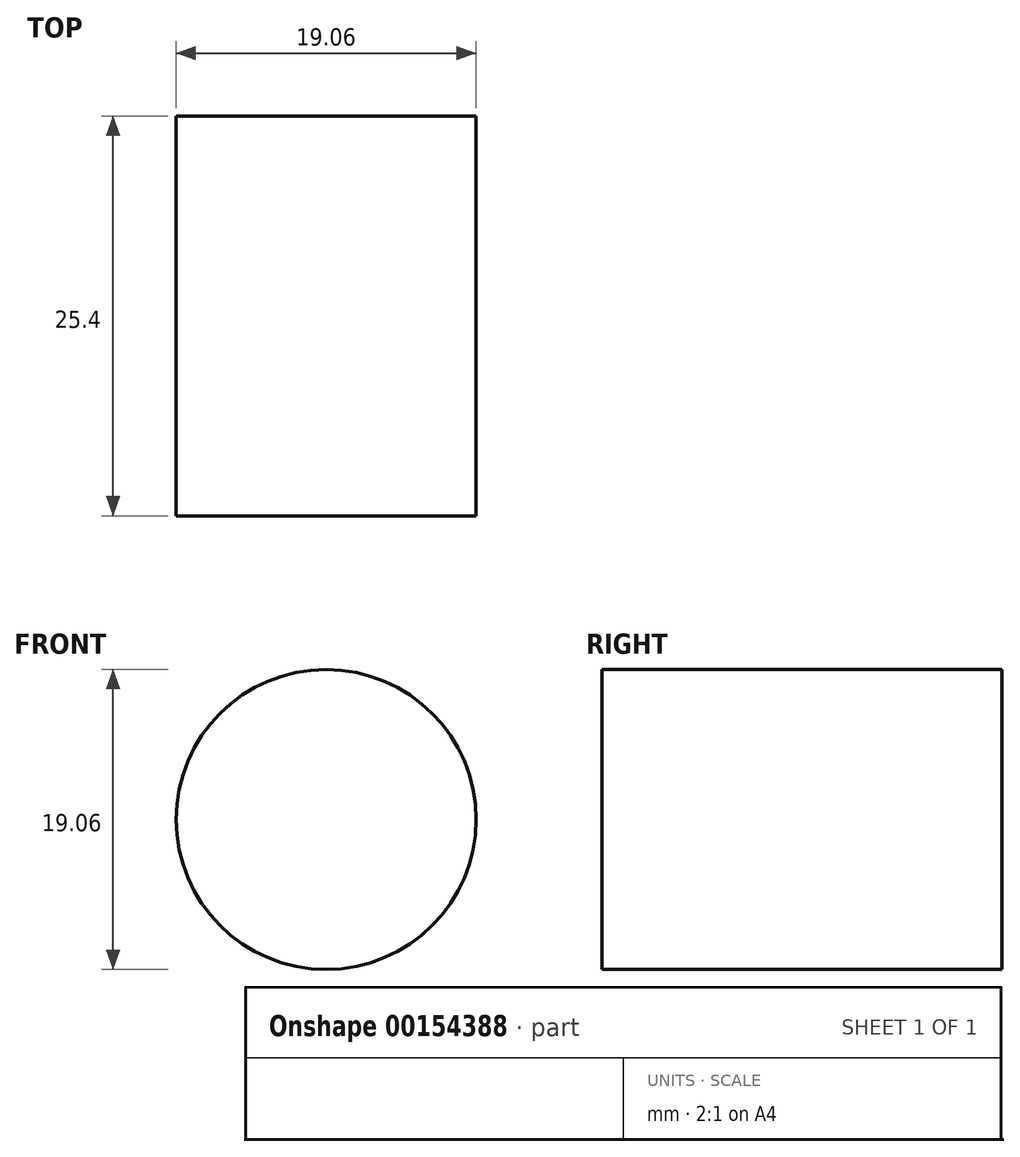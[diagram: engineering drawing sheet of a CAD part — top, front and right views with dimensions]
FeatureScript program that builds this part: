
annotation { "Feature Type Name" : "Feature", "Feature Type Description" : "" }
export const myFeature = defineFeature(function(context is Context, id is Id, definition is map)
    precondition{}
    {
        {
            var Q0;
            Q0=qCreatedBy(makeId("Front.planeOp"),FACE);
            var sketch = newSketch(context, id + "F0", { "sketchPlane" : qUnion([Q0])});
            skCircle(sketch, "E0", {"center": v(0, 0) * mm, "radius": 9.53 * mm});
            skSolve(sketch);
        }
        {
            var Q0;
            Q0=makeQuery(id+"F0.imprint","IMPRINT",FACE,{"disambiguationData":[TD([[makeQuery(id+"F0.imprint","IMPRINT",EDGE,{"derivedFrom":sQuery(id+"F0.wireOp",EDGE,"E0")}),1.0]])]});
            extrude(context, id + "F1", {"entities" : qUnion([Q0]), "depth" : 25.4 * mm});
        }
    });
